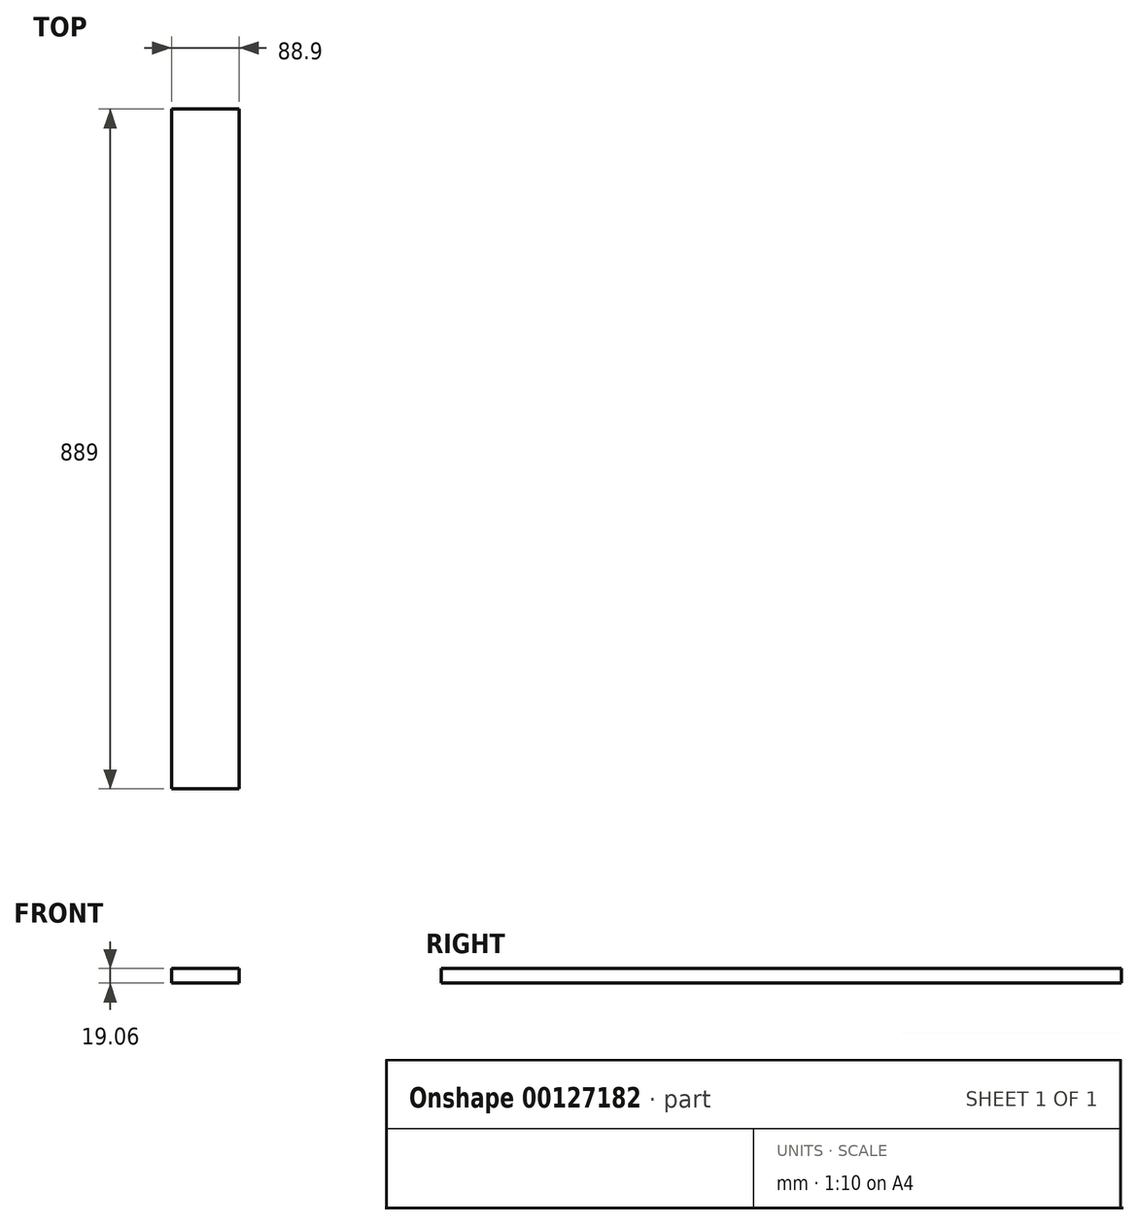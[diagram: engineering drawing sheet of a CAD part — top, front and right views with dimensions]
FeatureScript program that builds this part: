
annotation { "Feature Type Name" : "Feature", "Feature Type Description" : "" }
export const myFeature = defineFeature(function(context is Context, id is Id, definition is map)
    precondition{}
    {
        {
            var Q0;
            Q0=qCreatedBy(makeId("Front.planeOp"),FACE);
            var sketch = newSketch(context, id + "F0", { "sketchPlane" : qUnion([Q0])});
            skLineSegment(sketch, "E0.bottom", {"start": v(44.45, -9.52) * mm, "end": v(-44.45, -9.53) * mm});
            skLineSegment(sketch, "E0.top", {"start": v(44.45, 9.53) * mm, "end": v(-44.45, 9.53) * mm});
            skLineSegment(sketch, "E0.left", {"start": v(44.45, -9.52) * mm, "end": v(44.45, 9.53) * mm});
            skLineSegment(sketch, "E0.right", {"start": v(-44.45, -9.53) * mm, "end": v(-44.45, 9.53) * mm});
            skPoint(sketch, "E0.middle", {"position": v(0, 0) * mm});
            skSolve(sketch);
        }
        {
            var Q0;
            Q0=qSketchRegion(id+"F0",true);
            extrude(context, id + "F1", {"entities" : qUnion([Q0]), "depth" : 889 * mm});
        }
    });
